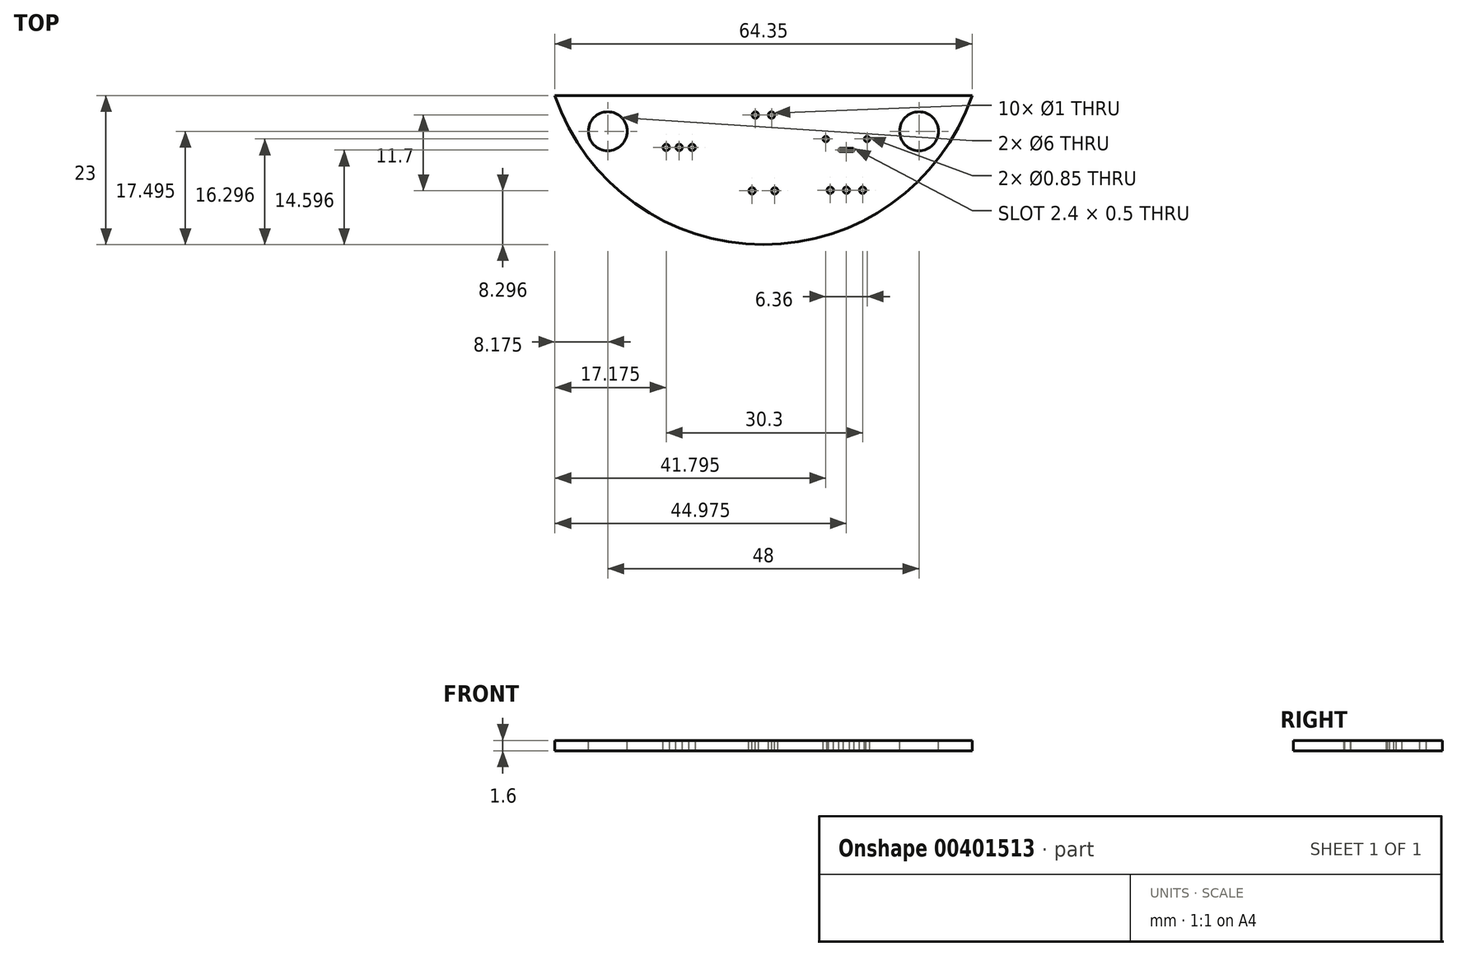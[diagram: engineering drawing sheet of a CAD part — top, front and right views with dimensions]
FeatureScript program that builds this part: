
annotation { "Feature Type Name" : "Feature", "Feature Type Description" : "" }
export const myFeature = defineFeature(function(context is Context, id is Id, definition is map)
    precondition{}
    {
        {
            var Q0;
            Q0=qCreatedBy(makeId("Top.planeOp"),FACE);
            var sketch = newSketch(context, id + "F0", { "sketchPlane" : qUnion([Q0])});
            skLineSegment(sketch, "E0.bottom", {"start": v(6.37, 29.29) * mm, "end": v(70.72, 29.29) * mm});
            skPoint(sketch, "E1.middle", {"position": v(38.54, 20.77) * mm});
            skPoint(sketch, "E2.orphan", {"position": v(18.04, 25.29) * mm});
            skPoint(sketch, "E3.orphan", {"position": v(59.04, 25.29) * mm});
            skArc(sketch, "E4", {"start": v(6.37, 29.29) * mm, "mid": v(38.54, 6.29) * mm, "end": v(70.72, 29.29) * mm});
            skSolve(sketch);
        }
        {
            var Q0;
            Q0=qSketchRegion(id+"F0",true);
            extrude(context, id + "F1", {"entities" : qUnion([Q0]), "depth" : 1.6 * mm});
        }
        {
            var Q0;
            Q0=makeQuery(id+"F1.opExtrude","CAP_FACE",FACE,{"disambiguationData":[OSD([sQuery(id+"F0.wireOp",EDGE,"E0.bottom"),sQuery(id+"F0.wireOp",EDGE,"E0.top"),sQuery(id+"F0.wireOp",EDGE,"E0.left"),sQuery(id+"F0.wireOp",EDGE,"E0.right"),sQuery(id+"F0.wireOp",EDGE,"E1.bottom"),sQuery(id+"F0.wireOp",EDGE,"E1.left"),sQuery(id+"F0.wireOp",EDGE,"E1.right")])],"isStart":false});
            var sketch = newSketch(context, id + "F2", { "sketchPlane" : qUnion([Q0])});
            skCircle(sketch, "E5", {"center": v(14.54, 23.79) * mm, "radius": 3 * mm});
            skLineSegment(sketch, "E6", {"start": v(38.54, 20.12) * mm, "end": v(38.54, 29.29) * mm, "construction": true});
            skCircle(sketch, "E7.MirrorC", {"center": v(62.54, 23.79) * mm, "radius": 3 * mm});
            skSolve(sketch);
        }
        {
            var Q0;
            Q0=qSketchRegion(id+"F2",true);
            extrude(context, id + "F3", {"entities" : qUnion([Q0]), "operationType" : NewBodyOperationType.REMOVE, "oppositeDirection" : true, "depth" : 3 * mm});
        }
        {
            var Q0;
            Q0=makeQuery(id+"F1.opExtrude","CAP_FACE",FACE,{"disambiguationData":[OSD([sQuery(id+"F0.wireOp",EDGE,"E0.bottom"),sQuery(id+"F0.wireOp",EDGE,"E0.top"),sQuery(id+"F0.wireOp",EDGE,"E0.left"),sQuery(id+"F0.wireOp",EDGE,"E0.right"),sQuery(id+"F0.wireOp",EDGE,"E1.bottom"),sQuery(id+"F0.wireOp",EDGE,"E1.left"),sQuery(id+"F0.wireOp",EDGE,"E1.right")])],"isStart":false});
            var sketch = newSketch(context, id + "F4", { "sketchPlane" : qUnion([Q0])});
            skCircle(sketch, "E8", {"center": v(23.54, 21.29) * mm, "radius": 0.5 * mm});
            skLineSegment(sketch, "E9", {"start": v(38.54, 22.32) * mm, "end": v(38.54, 29.29) * mm, "construction": true});
            skCircle(sketch, "E10.1.0.0", {"center": v(25.54, 21.29) * mm, "radius": 0.5 * mm});
            skLineSegment(sketch, "E10.direction1", {"start": v(23.54, 21.29) * mm, "end": v(25.54, 21.29) * mm, "construction": true});
            skCircle(sketch, "E11.0.2.0", {"center": v(27.54, 21.29) * mm, "radius": 0.5 * mm});
            skSolve(sketch);
        }
        {
            var Q0;
            Q0=makeQuery(id+"F1.opExtrude","CAP_FACE",FACE,{"disambiguationData":[OSD([sQuery(id+"F0.wireOp",EDGE,"E0.bottom"),sQuery(id+"F0.wireOp",EDGE,"E4")])],"isStart":false});
            var sketch = newSketch(context, id + "F5", { "sketchPlane" : qUnion([Q0])});
            skLineSegment(sketch, "E12", {"start": v(51.34, 15.9) * mm, "end": v(51.34, 29.22) * mm, "construction": true});
            skLineSegment(sketch, "E13", {"start": v(38.54, 6.29) * mm, "end": v(38.54, 25.84) * mm, "construction": true});
            skLineSegment(sketch, "E14", {"start": v(46.93, 22.59) * mm, "end": v(49.4, 22.59) * mm, "construction": true});
            skLineSegment(sketch, "E15", {"start": v(48.16, 22.59) * mm, "end": v(48.16, 25.77) * mm, "construction": true});
            skLineSegment(sketch, "E16", {"start": v(50.4, 20.89) * mm, "end": v(52.3, 20.89) * mm, "construction": true});
            skLineSegment(sketch, "E17", {"start": v(51.34, 20.89) * mm, "end": v(51.34, 19.92) * mm, "construction": true});
            skArc(sketch, "E18.0.startCap", {"start": v(50.4, 20.64) * mm, "mid": v(50.14, 20.89) * mm, "end": v(50.4, 21.14) * mm});
            skArc(sketch, "E18.0.endCap", {"start": v(52.3, 21.14) * mm, "mid": v(52.54, 20.89) * mm, "end": v(52.3, 20.64) * mm});
            skLineSegment(sketch, "E18.0.left", {"start": v(50.4, 21.14) * mm, "end": v(52.3, 21.14) * mm});
            skLineSegment(sketch, "E18.0.right", {"start": v(50.4, 20.64) * mm, "end": v(52.3, 20.64) * mm});
            skLineSegment(sketch, "E19", {"start": v(58.46, 21.44) * mm, "end": v(50.91, 21.44) * mm, "construction": true});
            skLineSegment(sketch, "E20", {"start": v(50.45, 21.94) * mm, "end": v(53.65, 21.94) * mm, "construction": true});
            skCircle(sketch, "E21", {"center": v(48.16, 22.59) * mm, "radius": 0.42 * mm});
            skCircle(sketch, "E22.MirrorC", {"center": v(54.52, 22.59) * mm, "radius": 0.42 * mm});
            skSolve(sketch);
        }
        {
            var Q0;
            Q0=makeQuery(id+"F1.opExtrude","CAP_FACE",FACE,{"disambiguationData":[OSD([sQuery(id+"F0.wireOp",EDGE,"E0.bottom"),sQuery(id+"F0.wireOp",EDGE,"E4")])],"isStart":false});
            var sketch = newSketch(context, id + "F6", { "sketchPlane" : qUnion([Q0])});
            skCircle(sketch, "E23", {"center": v(48.84, 14.69) * mm, "radius": 0.5 * mm});
            skCircle(sketch, "E24.1.0.0", {"center": v(53.84, 14.69) * mm, "radius": 0.5 * mm});
            skLineSegment(sketch, "E24.direction1", {"start": v(48.84, 14.69) * mm, "end": v(53.84, 14.69) * mm, "construction": true});
            skLineSegment(sketch, "E25", {"start": v(38.54, 6.29) * mm, "end": v(38.54, 17.65) * mm, "construction": true});
            skLineSegment(sketch, "E26", {"start": v(51.34, 14.69) * mm, "end": v(51.34, 23.7) * mm, "construction": true});
            skCircle(sketch, "E27", {"center": v(51.34, 14.69) * mm, "radius": 0.5 * mm});
            skSolve(sketch);
        }
        {
            var Q0;
            Q0=makeQuery(id+"F1.opExtrude","CAP_FACE",FACE,{"disambiguationData":[OSD([sQuery(id+"F0.wireOp",EDGE,"E0.bottom"),sQuery(id+"F0.wireOp",EDGE,"E4")])],"isStart":false});
            var sketch = newSketch(context, id + "F7", { "sketchPlane" : qUnion([Q0])});
            skCircle(sketch, "E28", {"center": v(37.3, 26.29) * mm, "radius": 0.5 * mm});
            skCircle(sketch, "E29.1.0.0", {"center": v(39.8, 26.29) * mm, "radius": 0.5 * mm});
            skLineSegment(sketch, "E29.direction1", {"start": v(37.3, 26.29) * mm, "end": v(39.8, 26.29) * mm, "construction": true});
            skLineSegment(sketch, "E30", {"start": v(38.54, 15.29) * mm, "end": v(38.54, 29.29) * mm, "construction": true});
            skLineSegment(sketch, "E31", {"start": v(38.54, 26.14) * mm, "end": v(38.54, 26.29) * mm, "construction": true});
            skSolve(sketch);
        }
        {
            var Q0;
            Q0=makeQuery(id+"F1.opExtrude","CAP_FACE",FACE,{"disambiguationData":[OSD([sQuery(id+"F0.wireOp",EDGE,"E0.bottom"),sQuery(id+"F0.wireOp",EDGE,"E4")])],"isStart":false});
            var sketch = newSketch(context, id + "F8", { "sketchPlane" : qUnion([Q0])});
            skCircle(sketch, "E32", {"center": v(36.8, 14.59) * mm, "radius": 0.5 * mm});
            skCircle(sketch, "E33.1.0.0", {"center": v(40.3, 14.59) * mm, "radius": 0.5 * mm});
            skLineSegment(sketch, "E33.direction1", {"start": v(36.8, 14.59) * mm, "end": v(40.3, 14.59) * mm, "construction": true});
            skLineSegment(sketch, "E34", {"start": v(38.54, 25.9) * mm, "end": v(38.54, 14.59) * mm, "construction": true});
            skSolve(sketch);
        }
        {
            var Q0;
            Q0=qSketchRegion(id+"F6",true);
            var Q1;
            Q1=qSketchRegion(id+"F7",true);
            var Q2;
            Q2=qSketchRegion(id+"F8",true);
            var Q3;
            Q3=qSketchRegion(id+"F5",true);
            var Q4;
            Q4=qSketchRegion(id+"F4",true);
            extrude(context, id + "F9", {"entities" : qUnion([Q0, Q1, Q2, Q3, Q4]), "operationType" : NewBodyOperationType.REMOVE, "oppositeDirection" : true, "depth" : 4 * mm});
        }
        {
            var Q0;
            Q0=makeQuery(id+"F1.opExtrude","CAP_FACE",FACE,{"disambiguationData":[OSD([sQuery(id+"F0.wireOp",EDGE,"E0.bottom"),sQuery(id+"F0.wireOp",EDGE,"E4")])],"isStart":true});
            var sketch = newSketch(context, id + "F10", { "sketchPlane" : qUnion([Q0])});
            skCircle(sketch, "E35", {"center": v(62.54, -23.79) * mm, "radius": 2.1 * mm});
            skLineSegment(sketch, "E36", {"start": v(38.54, -29.29) * mm, "end": v(38.54, 3.6) * mm, "construction": true});
            skCircle(sketch, "E37.MirrorC", {"center": v(14.54, -23.79) * mm, "radius": 2.1 * mm});
            skSolve(sketch);
        }
        {
            var Q0;
            Q0=qSketchRegion(id+"F10",true);
            extrude(context, id + "F11", {"entities" : qUnion([Q0]), "operationType" : NewBodyOperationType.REMOVE, "oppositeDirection" : true, "depth" : .2 * mm});
        }
    });
